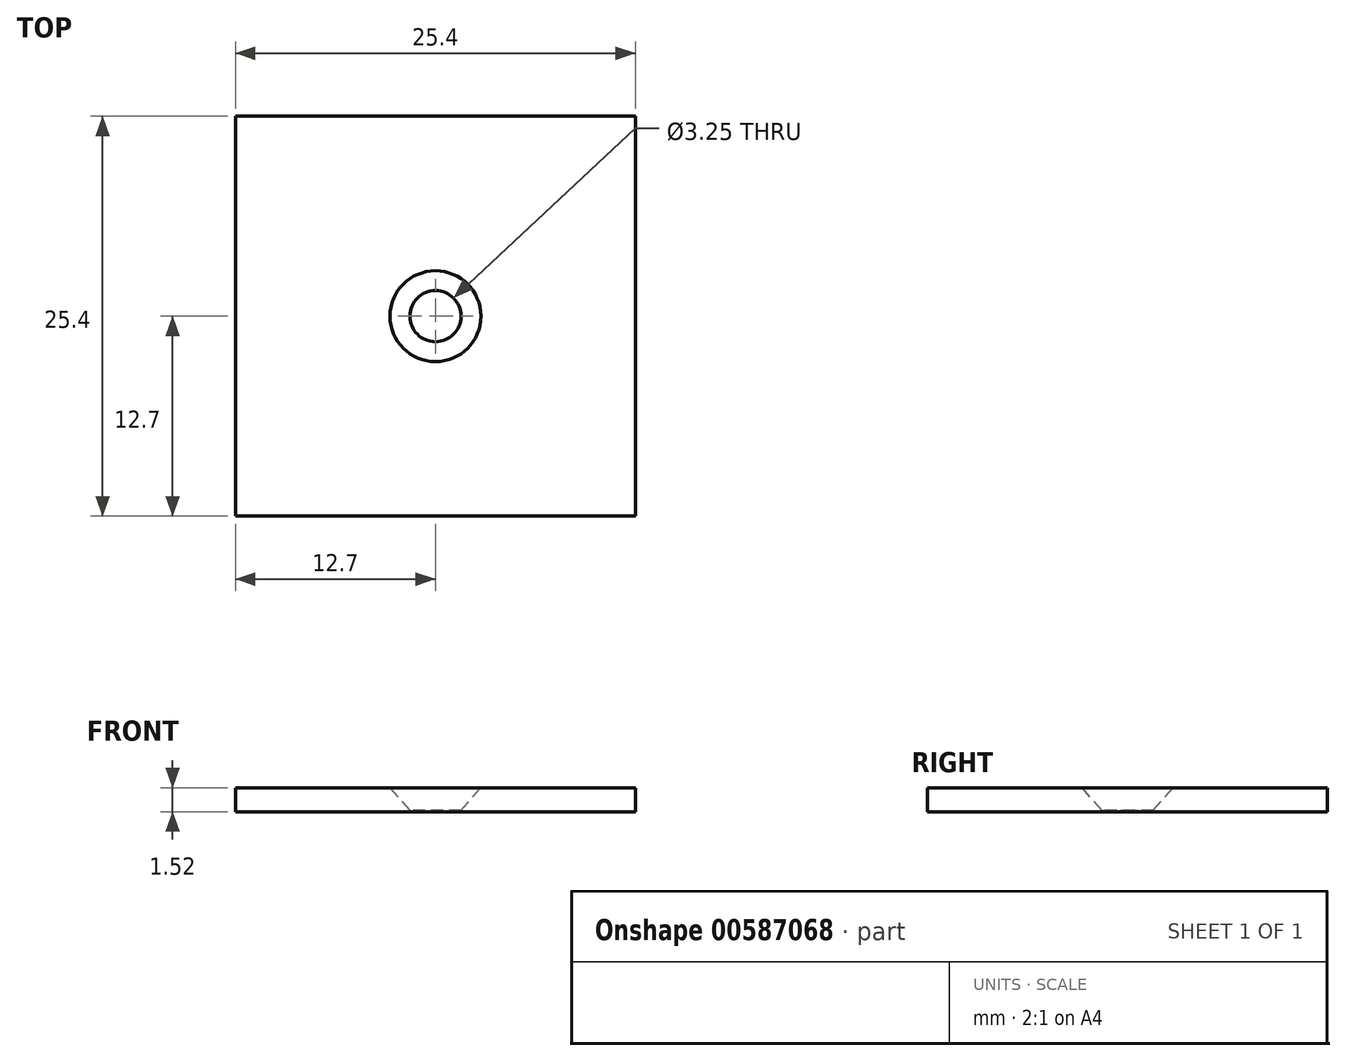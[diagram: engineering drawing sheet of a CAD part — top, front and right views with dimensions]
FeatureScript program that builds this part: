
annotation { "Feature Type Name" : "Feature", "Feature Type Description" : "" }
export const myFeature = defineFeature(function(context is Context, id is Id, definition is map)
    precondition{}
    {
        {
            var Q0;
            Q0=qCreatedBy(makeId("Top.planeOp"),FACE);
            var sketch = newSketch(context, id + "F0", { "sketchPlane" : qUnion([Q0])});
            skLineSegment(sketch, "E0.bottom", {"start": v(12.7, 12.7) * mm, "end": v(-12.7, 12.7) * mm});
            skLineSegment(sketch, "E0.top", {"start": v(12.7, -12.7) * mm, "end": v(-12.7, -12.7) * mm});
            skLineSegment(sketch, "E0.left", {"start": v(12.7, 12.7) * mm, "end": v(12.7, -12.7) * mm});
            skLineSegment(sketch, "E0.right", {"start": v(-12.7, 12.7) * mm, "end": v(-12.7, -12.7) * mm});
            skPoint(sketch, "E0.middle", {"position": v(0, 0) * mm});
            skCircle(sketch, "E1", {"center": v(0, 0) * mm, "radius": 1.63 * mm});
            skSolve(sketch);
        }
        {
            var Q0;
            Q0=makeQuery(id+"F0.imprint","IMPRINT",FACE,{"disambiguationData":[TD([[makeQuery(id+"F0.imprint","IMPRINT",EDGE,{"derivedFrom":sQuery(id+"F0.wireOp",EDGE,"E0.bottom")}),1.0]])]});
            extrude(context, id + "F1", {"entities" : qUnion([Q0]), "depth" : 1.52 * mm, "offsetDistance" : 25.4 * mm});
        }
        {
            var Q0;
            Q0=makeQuery(id+"F1.opExtrude","CAP_FACE",FACE,{"disambiguationData":[OSD([sQuery(id+"F0.wireOp",EDGE,"E0.bottom"),sQuery(id+"F0.wireOp",EDGE,"E0.top"),sQuery(id+"F0.wireOp",EDGE,"E0.left"),sQuery(id+"F0.wireOp",EDGE,"E0.right"),sQuery(id+"F0.wireOp",EDGE,"E1")])],"isStart":false});
            var sketch = newSketch(context, id + "F2", { "sketchPlane" : qUnion([Q0])});
            skCircle(sketch, "E2", {"center": v(0, 0) * mm, "radius": 2.9 * mm});
            skCircle(sketch, "E3", {"center": v(0, 0) * mm, "radius": 1.63 * mm});
            skSolve(sketch);
        }
        {
            var Q0;
            Q0=makeQuery(id+"F1.opExtrude","CAP_EDGE",EDGE,{"disambiguationData":[OSD([sQuery(id+"F0.wireOp",EDGE,"E1")])],"isStart":false});
            chamfer(context, id + "F3", {"entities" : qUnion([Q0]), "chamferType" : ChamferType.OFFSET_ANGLE, "width" : 1.45 * mm, "oppositeDirection" : false, "angle" : 41 * degree, "tangentPropagation" : true});
        }
    });
